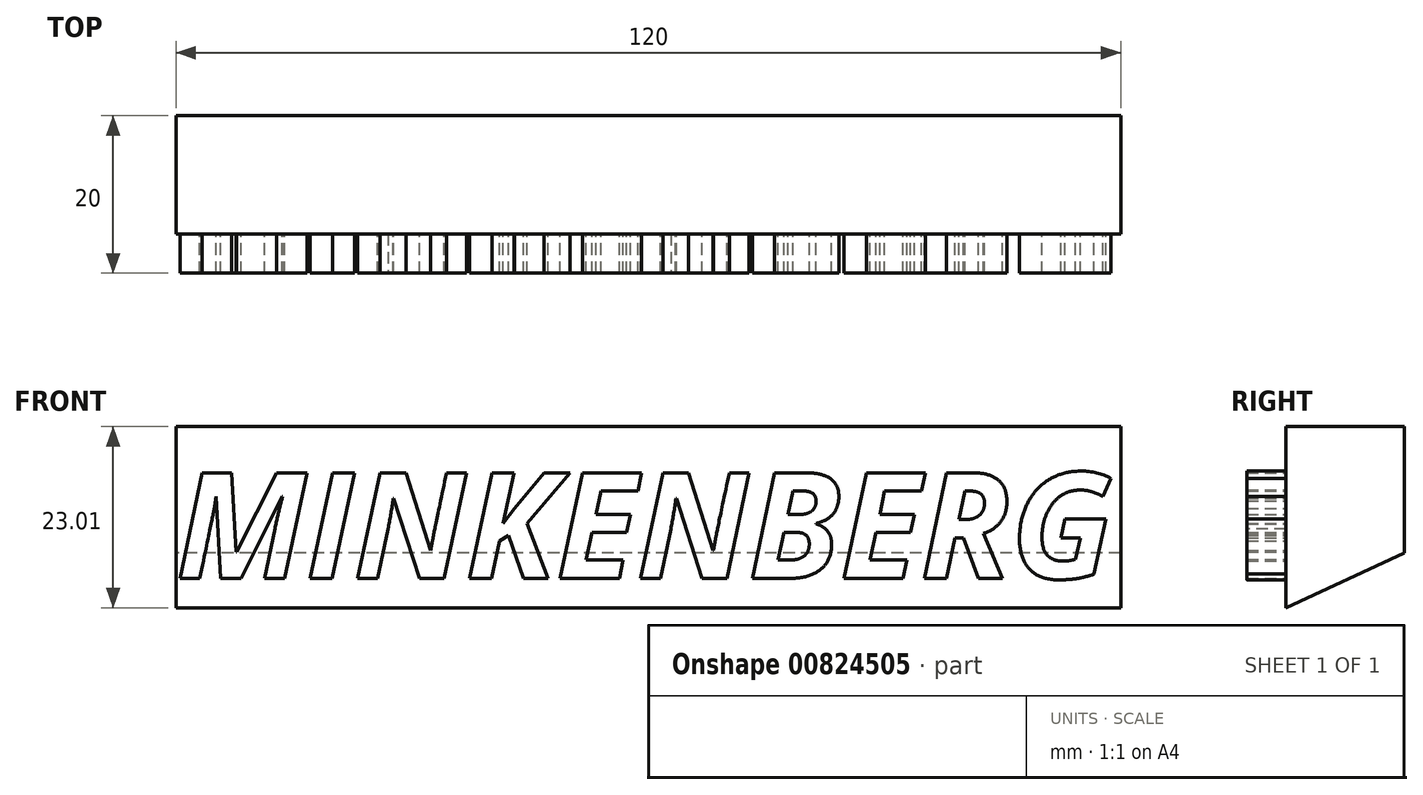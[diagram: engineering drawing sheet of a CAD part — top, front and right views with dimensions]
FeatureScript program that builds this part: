
annotation { "Feature Type Name" : "Feature", "Feature Type Description" : "" }
export const myFeature = defineFeature(function(context is Context, id is Id, definition is map)
    precondition{}
    {
        {
            var Q0;
            Q0=qCreatedBy(makeId("Front.planeOp"),FACE);
            var sketch = newSketch(context, id + "F0", { "sketchPlane" : qUnion([Q0])});
            skLineSegment(sketch, "E0.bottom", {"start": v(-60.13, 0) * mm, "end": v(59.87, 0) * mm});
            skLineSegment(sketch, "E0.top", {"start": v(-60.13, 30) * mm, "end": v(59.87, 30) * mm});
            skLineSegment(sketch, "E0.left", {"start": v(-60.13, 0) * mm, "end": v(-60.13, 30) * mm});
            skLineSegment(sketch, "E0.right", {"start": v(59.87, 0) * mm, "end": v(59.87, 30) * mm});
            skSolve(sketch);
        }
        {
            var Q0;
            Q0 = qSketchRegion(id + "F0", true);
            extrude(context, id + "F1", {"entities" : qUnion([Q0]), "depth" : 15 * mm, "offsetDistance" : 25 * mm});
        }
        {
            var Q0;
            Q0=makeQuery(id+"F1.opExtrude","CAP_FACE",FACE,{"disambiguationData":[OSD([sQuery(id+"F0.wireOp",EDGE,"E0.bottom"),sQuery(id+"F0.wireOp",EDGE,"E0.top"),sQuery(id+"F0.wireOp",EDGE,"E0.left"),sQuery(id+"F0.wireOp",EDGE,"E0.right")])],"isStart":false});
            var sketch = newSketch(context, id + "F2", { "sketchPlane" : qUnion([Q0])});
            skText(sketch, "E1", { "text": "MINKENBERG", "fontName": "OpenSans-BoldItalic.ttf"});
            const initialGuessF2  = {"E1": [-0.06013, 0.01072, 1, 0, 0.01354]};
            skSetInitialGuess(sketch, initialGuessF2);
            skSolve(sketch);
        }
        {
            var Q0;
            Q0 = qSketchRegion(id + "F2", true);
            extrude(context, id + "F3", {"entities" : qUnion([Q0]), "operationType" : NewBodyOperationType.ADD, "depth" : 5 * mm, "offsetDistance" : 25 * mm});
        }
        {
            var Q0;
            Q0=makeQuery(id+"F1.opExtrude","CAP_EDGE",EDGE,{"disambiguationData":[OSD([sQuery(id+"F0.wireOp",EDGE,"E0.bottom")])],"isStart":true});
            chamfer(context, id + "F4", {"entities" : qUnion([Q0]), "chamferType" : ChamferType.OFFSET_ANGLE, "width" : 30 * mm, "oppositeDirection" : false, "angle" : 25 * degree, "tangentPropagation" : true});
        }
    });
